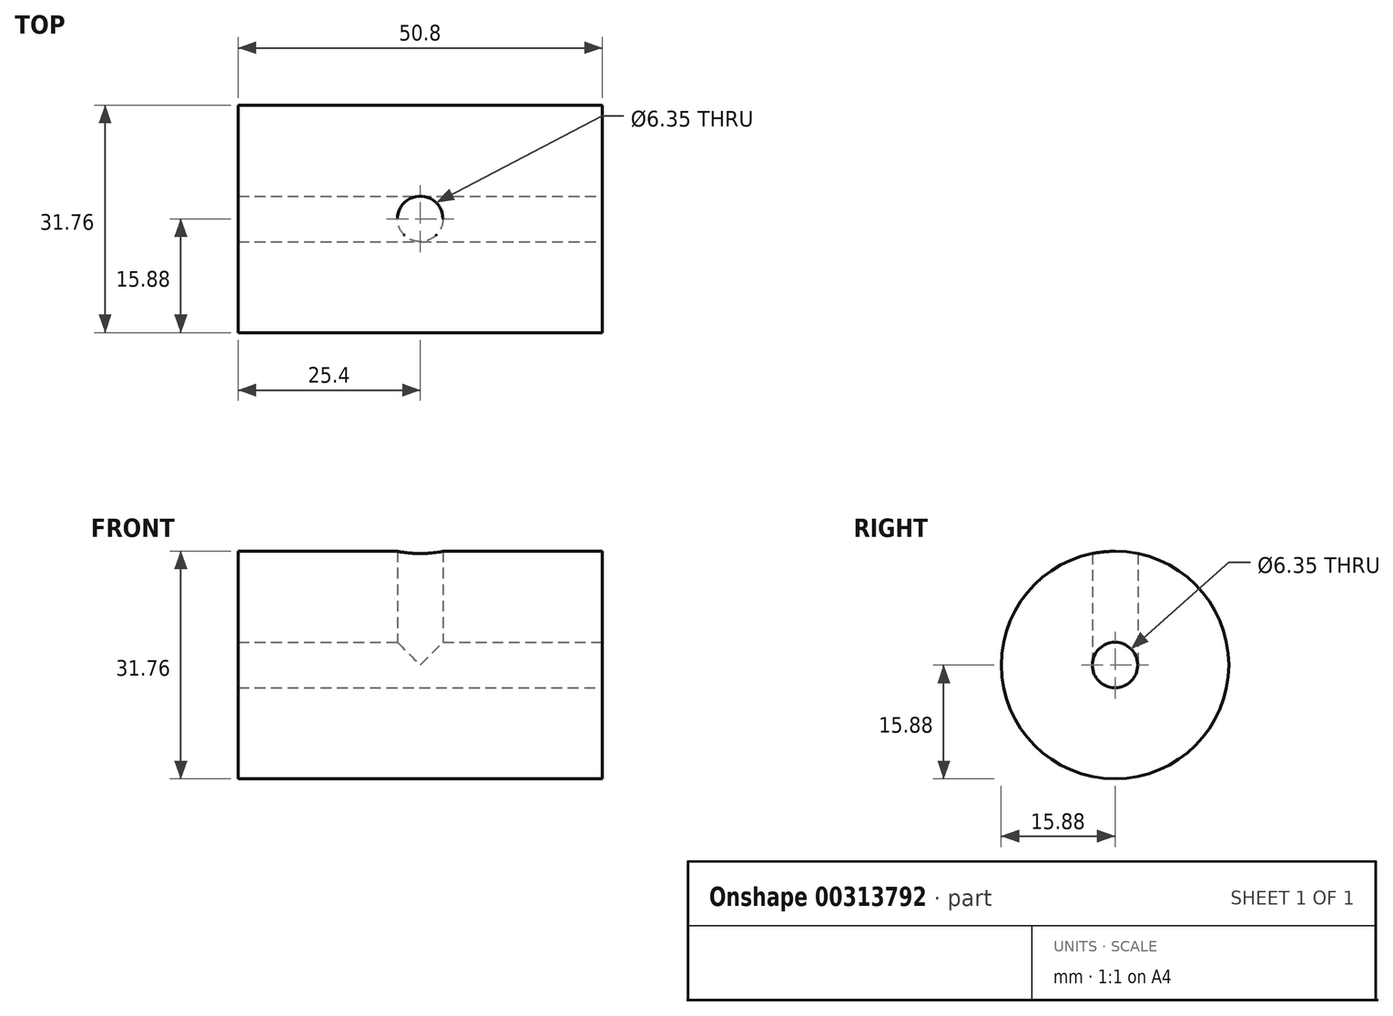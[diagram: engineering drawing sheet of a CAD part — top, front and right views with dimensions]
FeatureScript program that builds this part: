
annotation { "Feature Type Name" : "Feature", "Feature Type Description" : "" }
export const myFeature = defineFeature(function(context is Context, id is Id, definition is map)
    precondition{}
    {
        {
            var Q0;
            Q0=qCreatedBy(makeId("Front.planeOp"),FACE);
            var sketch = newSketch(context, id + "F0", { "sketchPlane" : qUnion([Q0])});
            skLineSegment(sketch, "E0", {"start": v(0, 0) * mm, "end": v(0, 62.73) * mm, "construction": true});
            skLineSegment(sketch, "E1", {"start": v(-65.33, 0) * mm, "end": v(83.25, 0) * mm, "construction": true});
            skLineSegment(sketch, "E2.bottom", {"start": v(-25.4, 15.88) * mm, "end": v(25.4, 15.88) * mm});
            skLineSegment(sketch, "E2.top", {"start": v(-25.4, 0) * mm, "end": v(25.4, 0) * mm});
            skLineSegment(sketch, "E2.left", {"start": v(-25.4, 15.88) * mm, "end": v(-25.4, 0) * mm});
            skLineSegment(sketch, "E2.right", {"start": v(25.4, 15.88) * mm, "end": v(25.4, 0) * mm});
            skSolve(sketch);
        }
        {
            var Q0;
            Q0=makeQuery(id+"F0.imprint","IMPRINT",FACE,{"disambiguationData":[TD([[makeQuery(id+"F0.imprint","IMPRINT",EDGE,{"derivedFrom":sQuery(id+"F0.wireOp",EDGE,"4xIOzpao-1mfH-gTLf-ZmZt-7D3k5552VkxL")}),-1.0]])]});
            var Q1;
            Q1=makeQuery(id+"F0.imprint","IMPRINT",FACE,{"disambiguationData":[TD([[makeQuery(id+"F0.imprint","IMPRINT",EDGE,{"derivedFrom":sQuery(id+"F0.wireOp",EDGE,"E2.bottom")}),-1.0]])]});
            var Q2;
            Q2=sQuery(id+"F0.wireOp",EDGE,"E1");
            revolve(context, id + "F1", {"entities" : qUnion([Q0, Q1]), "axis" : qUnion([Q2]), "revolveType" : RevolveType.FULL});
        }
        {
            var Q0;
            Q0=qCreatedBy(makeId("Top.planeOp"),FACE);
            var sketch = newSketch(context, id + "F2", { "sketchPlane" : qUnion([Q0])});
            skCircle(sketch, "E3", {"center": v(0, 0) * mm, "radius": 3.18 * mm});
            skSolve(sketch);
        }
        {
            var Q0;
            Q0 = qSketchRegion(id + "F2", true);
            extrude(context, id + "F3", {"entities" : qUnion([Q0]), "operationType" : NewBodyOperationType.REMOVE, "endBound" : BoundingType.THROUGH_ALL, "depth" : 25 * mm});
        }
        {
            var Q0;
            Q0=makeQuery(id+"F1.opRevolve","SWEPT_FACE",FACE,{"disambiguationData":[OSD([sQuery(id+"F0.wireOp",EDGE,"E2.right")])]});
            var sketch = newSketch(context, id + "F4", { "sketchPlane" : qUnion([Q0])});
            skCircle(sketch, "E4", {"center": v(0, 0) * mm, "radius": 3.18 * mm});
            skSolve(sketch);
        }
        {
            var Q0;
            Q0 = qSketchRegion(id + "F4", true);
            extrude(context, id + "F5", {"entities" : qUnion([Q0]), "operationType" : NewBodyOperationType.REMOVE, "endBound" : BoundingType.THROUGH_ALL, "oppositeDirection" : true, "depth" : 25.4 * mm});
        }
    });
